# Revit family: Gira_1002766
name_source: partatom
category: Electrical Fixtures
revit_build: Autodesk Revit 2017 (Build: 20160225_1515(x64)
units: mm (PartAtom-declared; Revit-internal decimal feet)

## family parameters
Cut with Voids When Loaded = No
Host = Face
Maintain Annotation Orientation = No
Part Type = Normal
Room Calculation Point = No
Round Connector Dimension = Use Diameter
Shared = No

## types (1)
- Cov.fr. 2-g w/o cb interm.fr. C Alu Gira Event Clear brown
    Available = No
    BIM (1) = https://media.stage.bim.site o.Mittelsteg.rfa?public/gira/36a6b08/Event_Rahmen_2fach o.Mittelsteg.rfa
    Category = Cover frame for domestic switching devices
    Colour = Brown
    Data sheet (1) = https://katalog.gira.de
    Default Elevation = 1219 mm
    Degree of protection (IP) = IP20
    Description = Cov.fr.2g w o cb i.fr.CAl EvCl BN,Gira Event Clear cover frame,brown with colour aluminium intermediate frame,2-gang without crossbar,Features:,- Shatter-proof.
    GTIN = 4010337070337
    HAN = 1002766
    Halogen free = Yes
    HeinzeBIM = https://bimportal.heinze.de
    Label space/information surface = No
    Manufacturer = Gira
    Manufacturer URL = https://www.gira.de
    Material = Plastic
    Material quality = Thermoplastic
    Mounting direction = Horizontal and vertical
    Name = Cov.fr. 2-g w/o cb interm.fr. C Alu Gira Event Clear brown
    Number of units = 2
    Number of units horizontal = 2
    Number of units vertical = 2
    Suitable for built-in installation = No
    Suitable for floor box = No
    Suitable for flush-mounted installation = Yes
    Suitable for wall duct = No
    Surface finishing = Glossy
    Surface protection = Other
    Transparent = No
    Type of fastening = Clamp mounting
    URL = http://katalog.gira.de
    With hinged lid = No
    With mounting grid = No

## geometry (parser evidence)
native form markers: Blend x2, Sweep x3
no freeform markers — native parametric forms only
